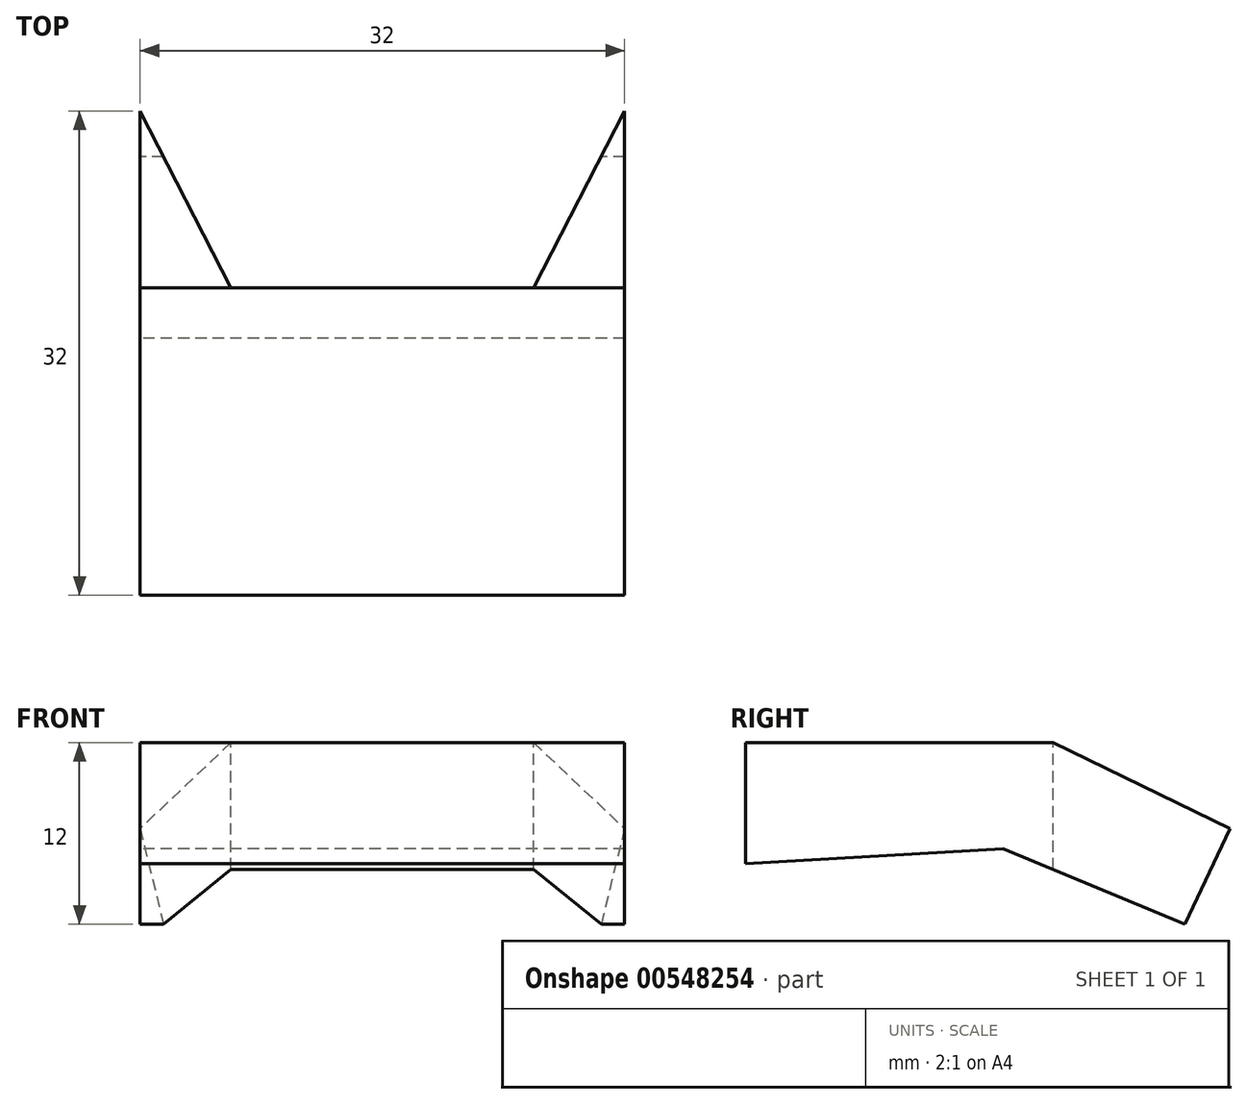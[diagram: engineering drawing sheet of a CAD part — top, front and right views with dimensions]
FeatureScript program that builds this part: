
annotation { "Feature Type Name" : "Feature", "Feature Type Description" : "" }
export const myFeature = defineFeature(function(context is Context, id is Id, definition is map)
    precondition{}
    {
        {
            var Q0;
            Q0=qCreatedBy(makeId("Right.planeOp"),FACE);
            var sketch = newSketch(context, id + "F0", { "sketchPlane" : qUnion([Q0])});
            skLineSegment(sketch, "E0", {"start": v(0, 0) * mm, "end": v(-17, -1) * mm});
            skLineSegment(sketch, "E1", {"start": v(-17, -1) * mm, "end": v(-17, 7) * mm});
            skLineSegment(sketch, "E2", {"start": v(-17, 7) * mm, "end": v(3.3, 7) * mm});
            skLineSegment(sketch, "E3", {"start": v(3.3, 7) * mm, "end": v(15, 1.32) * mm});
            skLineSegment(sketch, "E4", {"start": v(15, 1.32) * mm, "end": v(12, -5) * mm});
            skLineSegment(sketch, "E5", {"start": v(12, -5) * mm, "end": v(0, 0) * mm});
            skSolve(sketch);
        }
        {
            var Q0;
            Q0=makeQuery(id+"F0.imprint","IMPRINT",FACE,{"disambiguationData":[TD([[makeQuery(id+"F0.imprint","IMPRINT",EDGE,{"derivedFrom":sQuery(id+"F0.wireOp",EDGE,"E0")}),-1.0]])]});
            extrude(context, id + "F1", {"entities" : qUnion([Q0]), "endBound" : BoundingType.SYMMETRIC, "depth" : 32 * mm, "offsetDistance" : 25 * mm});
        }
        {
            var Q0;
            Q0=makeQuery(id+"F1.opExtrude","SWEPT_FACE",FACE,{"disambiguationData":[OSD([sQuery(id+"F0.wireOp",EDGE,"E2")])]});
            var sketch = newSketch(context, id + "F2", { "sketchPlane" : qUnion([Q0])});
            skLineSegment(sketch, "E6.0", {"start": v(16, 15) * mm, "end": v(-16, 15) * mm});
            skLineSegment(sketch, "E7", {"start": v(10, 3.3) * mm, "end": v(16, 15) * mm});
            skLineSegment(sketch, "E8", {"start": v(10, 3.3) * mm, "end": v(-10, 3.3) * mm});
            skLineSegment(sketch, "E9", {"start": v(-10, 3.3) * mm, "end": v(-16, 15) * mm});
            skSolve(sketch);
        }
        {
            var Q0;
            Q0=makeQuery(id+"F2.imprint","IMPRINT",FACE,{"disambiguationData":[TD([[makeQuery(id+"F2.imprint","IMPRINT",EDGE,{"derivedFrom":sQuery(id+"F2.wireOp",EDGE,"E6.0")}),1.0]])]});
            extrude(context, id + "F3", {"entities" : qUnion([Q0]), "operationType" : NewBodyOperationType.REMOVE, "oppositeDirection" : true, "depth" : 25 * mm, "offsetDistance" : 25 * mm});
        }
    });
